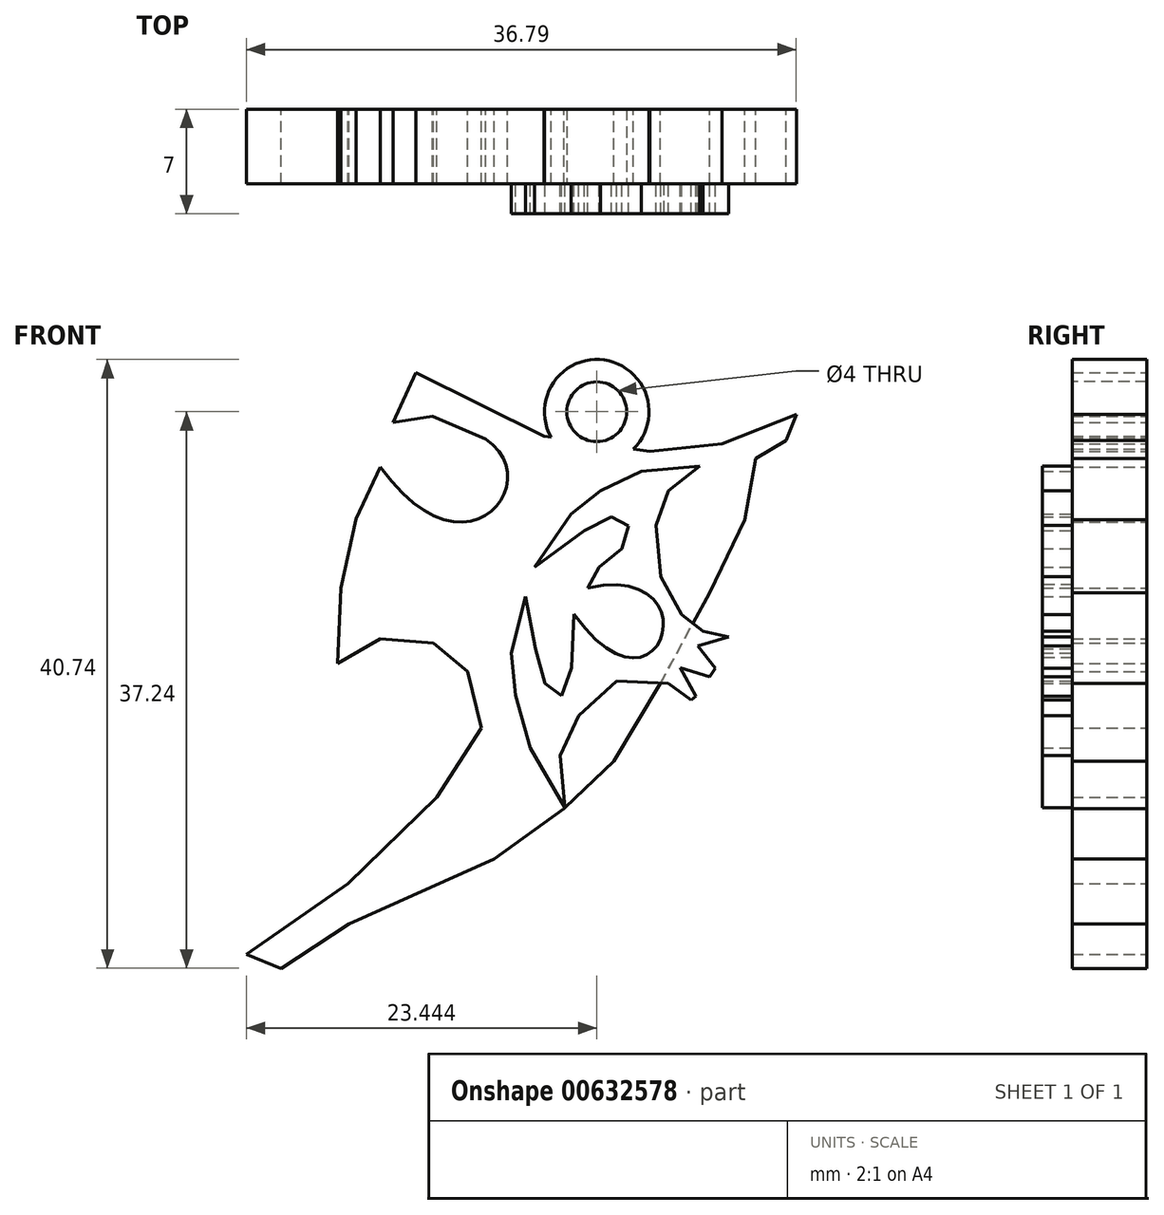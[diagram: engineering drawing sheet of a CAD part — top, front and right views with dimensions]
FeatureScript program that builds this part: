
annotation { "Feature Type Name" : "Feature", "Feature Type Description" : "" }
export const myFeature = defineFeature(function(context is Context, id is Id, definition is map)
    precondition{}
    {
        {
            var Q0;
            Q0=qCreatedBy(makeId("Front.planeOp"),FACE);
            var sketch = newSketch(context, id + "F0", { "sketchPlane" : qUnion([Q0])});
            skLineSegment(sketch, "E0", {"start": v(11.33, 0) * mm, "end": v(9.82, -3.32) * mm});
            skLineSegment(sketch, "E1", {"start": v(9.82, -3.32) * mm, "end": v(12.45, -2.9) * mm});
            skLineSegment(sketch, "E2", {"start": v(12.45, -2.9) * mm, "end": v(16, -4.44) * mm});
            skFitSpline(sketch, "E3", {"points": [v(16, -4.44) * mm, v(8.97, -6.31) * mm], "startDerivative": vector(12.63, -8.4) * mm, "endDerivative": vector(-17.05, 23.94) * mm});
            skLineSegment(sketch, "E4", {"start": v(8.97, -6.31) * mm, "end": v(7.35, -9.76) * mm});
            skLineSegment(sketch, "E5", {"start": v(7.35, -9.76) * mm, "end": v(6.34, -14.4) * mm});
            skLineSegment(sketch, "E6", {"start": v(6.34, -14.4) * mm, "end": v(6.11, -19.47) * mm});
            skLineSegment(sketch, "E7", {"start": v(6.11, -19.47) * mm, "end": v(8.97, -17.8) * mm});
            skLineSegment(sketch, "E8", {"start": v(8.97, -17.8) * mm, "end": v(12.53, -18.08) * mm});
            skLineSegment(sketch, "E9", {"start": v(12.53, -18.08) * mm, "end": v(14.8, -20) * mm});
            skLineSegment(sketch, "E10", {"start": v(14.8, -20) * mm, "end": v(15.71, -23.76) * mm});
            skLineSegment(sketch, "E11", {"start": v(15.71, -23.76) * mm, "end": v(12.74, -28.42) * mm});
            skLineSegment(sketch, "E12", {"start": v(12.74, -28.42) * mm, "end": v(6.8, -34.19) * mm});
            skLineSegment(sketch, "E13", {"start": v(6.8, -34.19) * mm, "end": v(0, -38.9) * mm});
            skLineSegment(sketch, "E14", {"start": v(0, -38.9) * mm, "end": v(2.34, -39.85) * mm});
            skLineSegment(sketch, "E15", {"start": v(2.34, -39.85) * mm, "end": v(6.87, -36.87) * mm});
            skLineSegment(sketch, "E16", {"start": v(6.87, -36.87) * mm, "end": v(16.59, -32.54) * mm});
            skLineSegment(sketch, "E17", {"start": v(16.59, -32.54) * mm, "end": v(21.24, -29.16) * mm});
            skLineSegment(sketch, "E18", {"start": v(21.24, -29.16) * mm, "end": v(24.57, -25.98) * mm});
            skLineSegment(sketch, "E19", {"start": v(24.57, -25.98) * mm, "end": v(27.7, -20.8) * mm});
            skLineSegment(sketch, "E20", {"start": v(27.7, -20.8) * mm, "end": v(30.98, -14.72) * mm});
            skLineSegment(sketch, "E21", {"start": v(30.98, -14.72) * mm, "end": v(33.36, -9.83) * mm});
            skLineSegment(sketch, "E22", {"start": v(33.36, -9.83) * mm, "end": v(34.09, -5.75) * mm});
            skLineSegment(sketch, "E23", {"start": v(34.09, -5.75) * mm, "end": v(36.12, -4.53) * mm});
            skLineSegment(sketch, "E24", {"start": v(36.12, -4.53) * mm, "end": v(36.8, -2.8) * mm});
            skLineSegment(sketch, "E25", {"start": v(36.8, -2.8) * mm, "end": v(31.8, -4.75) * mm});
            skLineSegment(sketch, "E26", {"start": v(31.8, -4.75) * mm, "end": v(27, -5.28) * mm});
            skLineSegment(sketch, "E27", {"start": v(27, -5.28) * mm, "end": v(19.92, -4.25) * mm});
            skLineSegment(sketch, "E28", {"start": v(19.92, -4.25) * mm, "end": v(11.33, 0) * mm});
            skSolve(sketch);
        }
        {
            var Q0;
            Q0=makeQuery(id+"F0.imprint","IMPRINT",FACE,{"disambiguationData":[TD([[makeQuery(id+"F0.imprint","IMPRINT",EDGE,{"derivedFrom":sQuery(id+"F0.wireOp",EDGE,"E0")}),1.0]])]});
            extrude(context, id + "F1", {"entities" : qUnion([Q0]), "depth" : 5 * mm, "offsetDistance" : 25 * mm});
        }
        {
            var Q0;
            Q0=makeQuery(id+"F1.opExtrude","CAP_FACE",FACE,{"disambiguationData":[OSD([sQuery(id+"F0.wireOp",EDGE,"E0"),sQuery(id+"F0.wireOp",EDGE,"E1"),sQuery(id+"F0.wireOp",EDGE,"E2"),sQuery(id+"F0.wireOp",EDGE,"E3"),sQuery(id+"F0.wireOp",EDGE,"E4"),sQuery(id+"F0.wireOp",EDGE,"E5"),sQuery(id+"F0.wireOp",EDGE,"E6"),sQuery(id+"F0.wireOp",EDGE,"E7"),sQuery(id+"F0.wireOp",EDGE,"E8"),sQuery(id+"F0.wireOp",EDGE,"E9"),sQuery(id+"F0.wireOp",EDGE,"E10"),sQuery(id+"F0.wireOp",EDGE,"E11"),sQuery(id+"F0.wireOp",EDGE,"E12"),sQuery(id+"F0.wireOp",EDGE,"E13"),sQuery(id+"F0.wireOp",EDGE,"E14"),sQuery(id+"F0.wireOp",EDGE,"E15"),sQuery(id+"F0.wireOp",EDGE,"E16"),sQuery(id+"F0.wireOp",EDGE,"E17"),sQuery(id+"F0.wireOp",EDGE,"E18"),sQuery(id+"F0.wireOp",EDGE,"E19"),sQuery(id+"F0.wireOp",EDGE,"E20"),sQuery(id+"F0.wireOp",EDGE,"E21"),sQuery(id+"F0.wireOp",EDGE,"E22"),sQuery(id+"F0.wireOp",EDGE,"E23"),sQuery(id+"F0.wireOp",EDGE,"E24"),sQuery(id+"F0.wireOp",EDGE,"E25"),sQuery(id+"F0.wireOp",EDGE,"E26"),sQuery(id+"F0.wireOp",EDGE,"E27"),sQuery(id+"F0.wireOp",EDGE,"E28")])],"isStart":false});
            var sketch = newSketch(context, id + "F2", { "sketchPlane" : qUnion([Q0])});
            skLineSegment(sketch, "E29", {"start": v(19.28, -13) * mm, "end": v(21.73, -9.45) * mm});
            skLineSegment(sketch, "E30", {"start": v(21.73, -9.45) * mm, "end": v(23.7, -7.9) * mm});
            skLineSegment(sketch, "E31", {"start": v(23.7, -7.9) * mm, "end": v(26.41, -6.6) * mm});
            skLineSegment(sketch, "E32", {"start": v(26.41, -6.6) * mm, "end": v(30.34, -6.24) * mm});
            skLineSegment(sketch, "E33", {"start": v(30.34, -6.24) * mm, "end": v(28.24, -7.9) * mm});
            skLineSegment(sketch, "E34", {"start": v(28.24, -7.9) * mm, "end": v(27.41, -10.2) * mm});
            skLineSegment(sketch, "E35", {"start": v(27.41, -10.2) * mm, "end": v(27.71, -13.65) * mm});
            skLineSegment(sketch, "E36", {"start": v(27.71, -13.65) * mm, "end": v(29.12, -16.18) * mm});
            skLineSegment(sketch, "E37", {"start": v(29.12, -16.18) * mm, "end": v(30.57, -17.28) * mm});
            skLineSegment(sketch, "E38", {"start": v(30.57, -17.28) * mm, "end": v(32.27, -17.66) * mm});
            skLineSegment(sketch, "E39", {"start": v(32.27, -17.66) * mm, "end": v(30.22, -18.29) * mm});
            skLineSegment(sketch, "E40", {"start": v(30.22, -18.29) * mm, "end": v(31.38, -19.77) * mm});
            skLineSegment(sketch, "E41", {"start": v(31.38, -19.77) * mm, "end": v(30.98, -20.34) * mm});
            skLineSegment(sketch, "E42", {"start": v(30.98, -20.34) * mm, "end": v(29.02, -19.74) * mm});
            skLineSegment(sketch, "E43", {"start": v(29.02, -19.74) * mm, "end": v(30.07, -21.65) * mm});
            skLineSegment(sketch, "E44", {"start": v(30.07, -21.65) * mm, "end": v(29.76, -21.9) * mm});
            skLineSegment(sketch, "E45", {"start": v(29.76, -21.9) * mm, "end": v(28.25, -20.8) * mm});
            skLineSegment(sketch, "E46", {"start": v(28.25, -20.8) * mm, "end": v(24.78, -20.63) * mm});
            skLineSegment(sketch, "E47", {"start": v(24.78, -20.63) * mm, "end": v(22.23, -22.94) * mm});
            skLineSegment(sketch, "E48", {"start": v(22.23, -22.94) * mm, "end": v(21, -25.62) * mm});
            skLineSegment(sketch, "E49", {"start": v(21, -25.62) * mm, "end": v(21.31, -29.1) * mm});
            skLineSegment(sketch, "E50", {"start": v(21.31, -29.1) * mm, "end": v(19, -25.1) * mm});
            skLineSegment(sketch, "E51", {"start": v(19, -25.1) * mm, "end": v(18, -21.58) * mm});
            skLineSegment(sketch, "E52", {"start": v(18, -21.58) * mm, "end": v(17.72, -18.75) * mm});
            skLineSegment(sketch, "E53", {"start": v(17.72, -18.75) * mm, "end": v(18.67, -14.96) * mm});
            skLineSegment(sketch, "E54", {"start": v(18.67, -14.96) * mm, "end": v(19.34, -18.48) * mm});
            skLineSegment(sketch, "E55", {"start": v(19.34, -18.48) * mm, "end": v(19.97, -20.8) * mm});
            skLineSegment(sketch, "E56", {"start": v(19.97, -20.8) * mm, "end": v(21.1, -21.62) * mm});
            skLineSegment(sketch, "E57", {"start": v(21.1, -21.62) * mm, "end": v(21.76, -19.74) * mm});
            skLineSegment(sketch, "E58", {"start": v(21.76, -19.74) * mm, "end": v(21.91, -16.14) * mm});
            skFitSpline(sketch, "E59", {"points": [v(21.91, -16.14) * mm, v(22.84, -14.4) * mm], "startDerivative": vector(17.69, -24.7) * mm, "endDerivative": vector(-25.52, -5.62) * mm});
            skLineSegment(sketch, "E60", {"start": v(22.84, -14.4) * mm, "end": v(23.6, -13) * mm});
            skLineSegment(sketch, "E61", {"start": v(23.6, -13) * mm, "end": v(25.11, -11.76) * mm});
            skLineSegment(sketch, "E62", {"start": v(25.11, -11.76) * mm, "end": v(25.55, -10.25) * mm});
            skLineSegment(sketch, "E63", {"start": v(25.55, -10.25) * mm, "end": v(24.44, -9.64) * mm});
            skLineSegment(sketch, "E64", {"start": v(24.44, -9.64) * mm, "end": v(22.6, -10.56) * mm});
            skLineSegment(sketch, "E65", {"start": v(22.6, -10.56) * mm, "end": v(19.28, -13) * mm});
            skSolve(sketch);
        }
        {
            var Q0;
            Q0=makeQuery(id+"F2.imprint","IMPRINT",FACE,{"disambiguationData":[TD([[makeQuery(id+"F2.imprint","IMPRINT",EDGE,{"derivedFrom":sQuery(id+"F2.wireOp",EDGE,"E29")}),-1.0]])]});
            var Q1;
            {var subQ4=sQuery(id+"F2.wireOp",EDGE,"E38");Q1=makeQuery(id+"F2.imprint","IMPRINT",FACE,{"disambiguationData":[TD([[makeQuery(id+"F2.imprint","IMPRINT",EDGE,{"derivedFrom":subQ4}),-1.0]])]});}
            extrude(context, id + "F3", {"entities" : qUnion([Q0, Q1]), "operationType" : NewBodyOperationType.ADD, "depth" : 2 * mm, "offsetDistance" : 25 * mm});
        }
        {
            var Q0;
            Q0=qCreatedBy(makeId("Front.planeOp"),FACE);
            var sketch = newSketch(context, id + "F4", { "sketchPlane" : qUnion([Q0])});
            skCircle(sketch, "E66", {"center": v(23.44, -2.61) * mm, "radius": 3.5 * mm});
            skSolve(sketch);
        }
        {
            var Q0;
            Q0 = qSketchRegion(id + "F4", true);
            extrude(context, id + "F5", {"entities" : qUnion([Q0]), "operationType" : NewBodyOperationType.ADD, "depth" : 5 * mm, "offsetDistance" : 25 * mm});
        }
        {
            var Q0;
            {var subQ1=sQuery(id+"F0.wireOp",EDGE,"E26");var subQ3=sQuery(id+"F0.wireOp",EDGE,"E25");var subQ5=sQuery(id+"F0.wireOp",EDGE,"E24");var subQ7=sQuery(id+"F0.wireOp",EDGE,"E23");var subQ9=sQuery(id+"F0.wireOp",EDGE,"E22");var subQ11=sQuery(id+"F0.wireOp",EDGE,"E21");var subQ13=sQuery(id+"F0.wireOp",EDGE,"E20");var subQ15=sQuery(id+"F0.wireOp",EDGE,"E28");var subQ34=sQuery(id+"F0.wireOp",EDGE,"E17");var subQ35=sQuery(id+"F0.wireOp",EDGE,"E27");var subQ36=sQuery(id+"F0.wireOp",EDGE,"E16");var subQ37=sQuery(id+"F0.wireOp",EDGE,"E8");var subQ38=sQuery(id+"F0.wireOp",EDGE,"E7");var subQ39=sQuery(id+"F0.wireOp",EDGE,"E6");var subQ40=sQuery(id+"F0.wireOp",EDGE,"E5");var subQ41=sQuery(id+"F0.wireOp",EDGE,"E4");var subQ42=sQuery(id+"F0.wireOp",EDGE,"E3");var subQ43=sQuery(id+"F0.wireOp",EDGE,"E0");var subQ44=sQuery(id+"F0.wireOp",EDGE,"E18");var subQ45=sQuery(id+"F0.wireOp",EDGE,"E15");var subQ46=sQuery(id+"F0.wireOp",EDGE,"E14");var subQ47=sQuery(id+"F0.wireOp",EDGE,"E13");var subQ48=sQuery(id+"F0.wireOp",EDGE,"E12");var subQ49=sQuery(id+"F0.wireOp",EDGE,"E11");var subQ50=sQuery(id+"F0.wireOp",EDGE,"E10");var subQ51=sQuery(id+"F0.wireOp",EDGE,"E9");var subQ52=sQuery(id+"F0.wireOp",EDGE,"E2");var subQ53=sQuery(id+"F0.wireOp",EDGE,"E1");var subQ54=makeQuery(id+"F1.opExtrude","CAP_FACE",FACE,{"disambiguationData":[OSD([subQ43,subQ53,subQ52,subQ42,subQ41,subQ40,subQ39,subQ38,subQ37,subQ51,subQ50,subQ49,subQ48,subQ47,subQ46,subQ45,subQ36,subQ34,subQ44,sQuery(id+"F0.wireOp",EDGE,"E19"),subQ13,subQ11,subQ9,subQ7,subQ5,subQ3,subQ1,subQ35,subQ15])],"isStart":false});Q0=makeQuery(id+"F5.boolean.opBoolean","MERGE",FACE,{"derivedFrom":[makeQuery(id+"F3.boolean.opBoolean","SPLIT",FACE,{"disambiguationData":[TD([makeQuery(id+"F1.opExtrude","SWEPT_FACE",FACE,{"disambiguationData":[OSD([subQ43])]})])],"derivedFrom":subQ54}),makeQuery(id+"F5.opExtrude","CAP_FACE",FACE,{"disambiguationData":[OSD([sQuery(id+"F4.wireOp",EDGE,"E66")])],"isStart":false})]});}
            var sketch = newSketch(context, id + "F6", { "sketchPlane" : qUnion([Q0])});
            skCircle(sketch, "E67", {"center": v(23.44, -2.61) * mm, "radius": 2 * mm});
            skSolve(sketch);
        }
        {
            var Q0;
            Q0 = qSketchRegion(id + "F6", true);
            extrude(context, id + "F7", {"entities" : qUnion([Q0]), "operationType" : NewBodyOperationType.REMOVE, "oppositeDirection" : true, "depth" : 5000 * mm, "offsetDistance" : 25 * mm});
        }
    });
